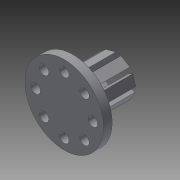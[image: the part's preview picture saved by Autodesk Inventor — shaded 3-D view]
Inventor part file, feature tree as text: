
AUTODESK INVENTOR PART (.ipt)
format: ipt  version: 2013 (Build 170138000, 138)  size: 199,168 bytes
history: native  units: mm
features: sketch x3, extrude x2, fillet x2, hole x1, pattern_circular x1
ambient origin geometry x8: Origin, YZ Plane, XZ Plane, XY Plane, X Axis, Y Axis, Z Axis, Center Point
feature tree (9):
  extrude  "Extrusion5"  Depth=6.0mm TaperAngle=0.0deg
  hole  "Hole2"  [1 undecoded]
  extrude  "Extrusion6"  Depth=4.0mm
  fillet  "Fillet4"  Radius=10.0mm
  fillet  "Fillet5"  Radius=30.0mm
  pattern_circular  "Circular Pattern1"  [2 undecoded]
  sketch  "Sketch7"  dims[d35=55.0mm d36=6.0mm d37=0.0mm]
  sketch  "Sketch8"  dims[d38=20.0mm d39=80.0mm d41=360.0deg]
  sketch  "Sketch9"  dims[d43=6.6mm d44=6.0mm d45=12.6mm d46=2.0mm d47=90.0deg d48=8.0mm d49=20.594885mm d59=4.0mm d60=10.0mm d65=30.0mm d66=0.0mm d73=0.5mm d74=80.0mm d75=360.0deg d77=3.0mm]
note: 3 required parameter values undecoded (feature->parameter linkage not recoverable at this tier; creation-order binding heuristic only, values carry confidence <= 0.55)
